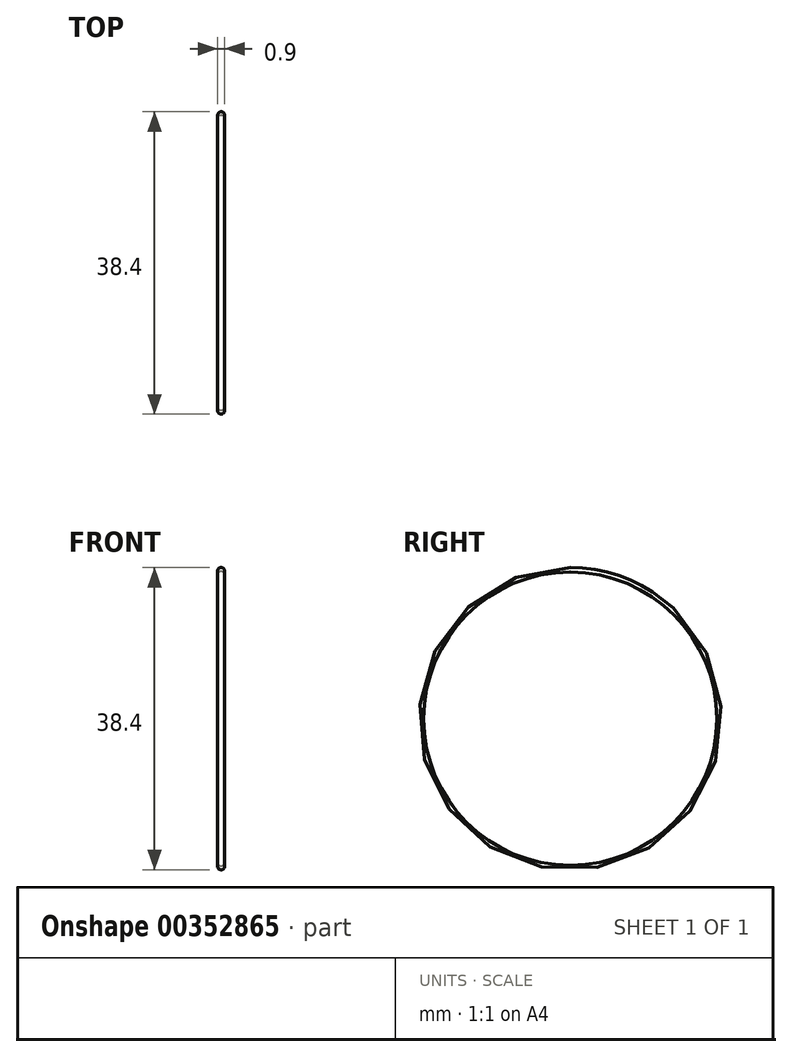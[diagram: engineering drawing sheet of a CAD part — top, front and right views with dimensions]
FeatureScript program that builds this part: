
annotation { "Feature Type Name" : "Feature", "Feature Type Description" : "" }
export const myFeature = defineFeature(function(context is Context, id is Id, definition is map)
    precondition{}
    {
        {
            var Q0;
            Q0=qCreatedBy(makeId("Right.planeOp"),FACE);
            var sketch = newSketch(context, id + "F0", { "sketchPlane" : qUnion([Q0])});
            skCircle(sketch, "E0", {"center": v(-44.45, -25.4) * mm, "radius": 19.05 * mm});
            skPoint(sketch, "E1.start.orphan", {"position": v(0, 0) * mm});
            skPoint(sketch, "E2.MirrorCS.end.orphan", {"position": v(44.45, 0) * mm});
            skPoint(sketch, "E3.MirrorCS.end.orphan", {"position": v(44.45, -25.4) * mm});
            skPoint(sketch, "E4.orphan", {"position": v(-44.45, 0) * mm});
            skSolve(sketch);
        }
        {
            var Q0;
            Q0=qCreatedBy(makeId("Front.planeOp"),FACE);
            cPlane(context, id + "F1", {"entities" : qUnion([Q0]), "cplaneType" : CPlaneType.OFFSET, "offset" : 44.45 * mm, "width" : 152.4 * mm, "height" : 152.4 * mm});
        }
        {
            var Q0;
            Q0=qCreatedBy(id+"F1.planeOp",FACE);
            var sketch = newSketch(context, id + "F2", { "sketchPlane" : qUnion([Q0])});
            skPoint(sketch, "E5.center.orphan", {"position": v(0, -6.79) * mm});
            skArc(sketch, "E6", {"start": v(0.43, -6.79) * mm, "mid": v(0, -6.2) * mm, "end": v(-0.43, -6.79) * mm});
            skFitSpline(sketch, "E7", {"points": [v(-0.43, -6.79) * mm, v(0, -6.65) * mm, v(0.43, -6.79) * mm], "startDerivative": vector(0.86, 0.4) * mm, "endDerivative": vector(0.86, -0.4) * mm});
            skSolve(sketch);
        }
        {
            var Q0;
            Q0=makeQuery(id+"F2.imprint","IMPRINT",FACE,{"disambiguationData":[TD([[makeQuery(id+"F2.imprint","IMPRINT",EDGE,{"derivedFrom":sQuery(id+"F2.wireOp",EDGE,"E5")}),1.0]])]});
            var Q1;
            Q1=makeQuery(id+"F2.imprint","IMPRINT",FACE,{"disambiguationData":[TD([[makeQuery(id+"F2.imprint","IMPRINT",EDGE,{"derivedFrom":sQuery(id+"F2.wireOp",EDGE,"E6")}),1.0]])]});
            var Q2;
            Q2=sQuery(id+"F0.wireOp",EDGE,"E0");
            sweep(context, id + "F3", {"profiles" : qUnion([Q0, Q1]), "path" : qUnion([Q2])});
        }
        {
            var Q0;
            Q0=qCreatedBy(makeId("Right.planeOp"),FACE);
            var sketch = newSketch(context, id + "F4", { "sketchPlane" : qUnion([Q0])});
            skLineSegment(sketch, "E8", {"start": v(0, 0) * mm, "end": v(-44.45, 0) * mm});
            skLineSegment(sketch, "E9", {"start": v(-44.45, 0) * mm, "end": v(-44.45, -25.4) * mm});
            skCircle(sketch, "E10", {"center": v(-44.45, -25.4) * mm, "radius": 1.27 * mm});
            skLineSegment(sketch, "E11.bottom", {"start": v(-63.29, -24.76) * mm, "end": v(-25.61, -24.76) * mm});
            skLineSegment(sketch, "E11.top", {"start": v(-63.29, -26.03) * mm, "end": v(-25.61, -26.03) * mm});
            skLineSegment(sketch, "E11.left", {"start": v(-63.29, -24.76) * mm, "end": v(-63.29, -26.03) * mm});
            skLineSegment(sketch, "E11.right", {"start": v(-25.61, -24.76) * mm, "end": v(-25.61, -26.03) * mm});
            skLineSegment(sketch, "E12.bottom", {"start": v(-43.82, -6.6) * mm, "end": v(-45.09, -6.6) * mm});
            skLineSegment(sketch, "E12.top", {"start": v(-43.82, -44.2) * mm, "end": v(-45.09, -44.2) * mm});
            skLineSegment(sketch, "E12.left", {"start": v(-43.82, -6.6) * mm, "end": v(-43.82, -44.2) * mm});
            skLineSegment(sketch, "E12.right", {"start": v(-45.09, -6.6) * mm, "end": v(-45.09, -44.2) * mm});
            skSolve(sketch);
        }
        {
            var Q0;
            Q0=sQuery(id+"F4.wireOp",EDGE,"E10");
            extrude(context, id + "F5", {"bodyType" : ToolBodyType.SURFACE, "surfaceEntities" : qUnion([Q0]), "endBound" : BoundingType.SYMMETRIC, "depth" : 0.5 * mm});
        }
    });
